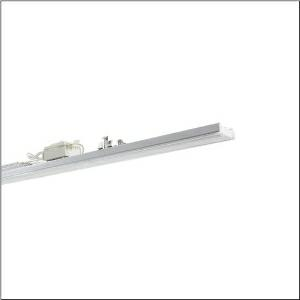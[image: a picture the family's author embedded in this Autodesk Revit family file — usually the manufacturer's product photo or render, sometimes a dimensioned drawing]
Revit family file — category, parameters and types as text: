
# Revit family: licross_r__11_recessed_mo_51tl1emn495g_cbfe
name_source: partatom
category: Lighting Fixtures
units: mm (PartAtom-declared; Revit-internal decimal feet)

## family parameters
Cut with Voids When Loaded = No
Host = Face
Light Source = No
Part Type = Normal
Room Calculation Point = No
Round Connector Dimension = Use Diameter
Shared = No

## types (1)
- --- (1 x LED, 9950 lm, 55.2 W, 4000K)
    Apparent Load = 55 VA
    CIE Flux Codes = 85 95 99 100 100
    Color Rendering = 80
    Color Temperature = 4000K
    Default Elevation = 1800 mm
    Description = Licross® 11 Recessed MO, luminaire insert, of sheet steel, coil coated, white, length: 1.500mm, width: 66mm, height: 67mm, LED rated luminous flux: 9.950lm, light colour: 840, control gear: ON/OFF Multilumen, with plug, 3-pole, with phase selection, mains connection: 220..240V, AC, 50/60Hz, rated input power: 55W, halogen-free wiring, primary light control with lens, of plastic, primary optical cover: cover, of PMMA, light emission: direct distribution, primary light characteristic: symmetric, protection rating (complete): IP40, insulation class (complete): insulation class I (protective earthing), certification: CE, ENEC, VDE, UKCA, protection symbol: D if used in an environment without relevant dust loads with corresponding accessories, impact resistance: IK06, permissible ambient temperature for indoor applications: -35..+40°C, corresponds to IFS (International Featured Standards) requirements for safety and quality in the food industry, reducing of maximum allowable ambient temperature of 5°C with ceiling mounting, packaging unit: 1 piece
    Height = 58 mm
    Lamp = 1 x LED
    Lamp Light Flux = 9950 lm
    Lamp Power = 55.2 W
    Lamp count = 1
    Length = 1500 mm
    Luminous efficacy = 180 lm/W
    Manufacturer = Siteco
    ModVariant = No
    Model = 51TL1EMN495G
    Mounting Place = Ceiling
    Mounting Type = Pendant
    Number of Poles = 1
    OnlyDefault = Yes
    Power Factor = 1
    Product Name = Licross® 11 Recessed MO
    Product group = luminaire insert
    ProductGroupID = 902
    Protection Class = Protection class I
    Protection Degree = IP 40
    RLX_Detail_Level = 1
    RLX_Emergency_Light_Flux = 0 lm
    RLX_Emergency_Type = 0
    RLX_Emergency_Type_DB = No
    RlxData = <blob elided: 22257 chars, md5=544f59b3>
    Socket = socket
    Standby Power = 0 W
    System Light Flux = 9950 lm
    System Power = 55 W
    Type Comments = factory setting: luminous flux: 100 % | (A | C | E) | 126 mA
    Type Image = l_1296930.jpg
    URL = http://relux.com
    VarID = @adj_084326
    Voltage = 0 V
    Weight = 0.00 kg
    Width = 66 mm

## geometry (parser evidence)
native form markers: Blend x4, Sweep x11
no freeform markers — native parametric forms only
